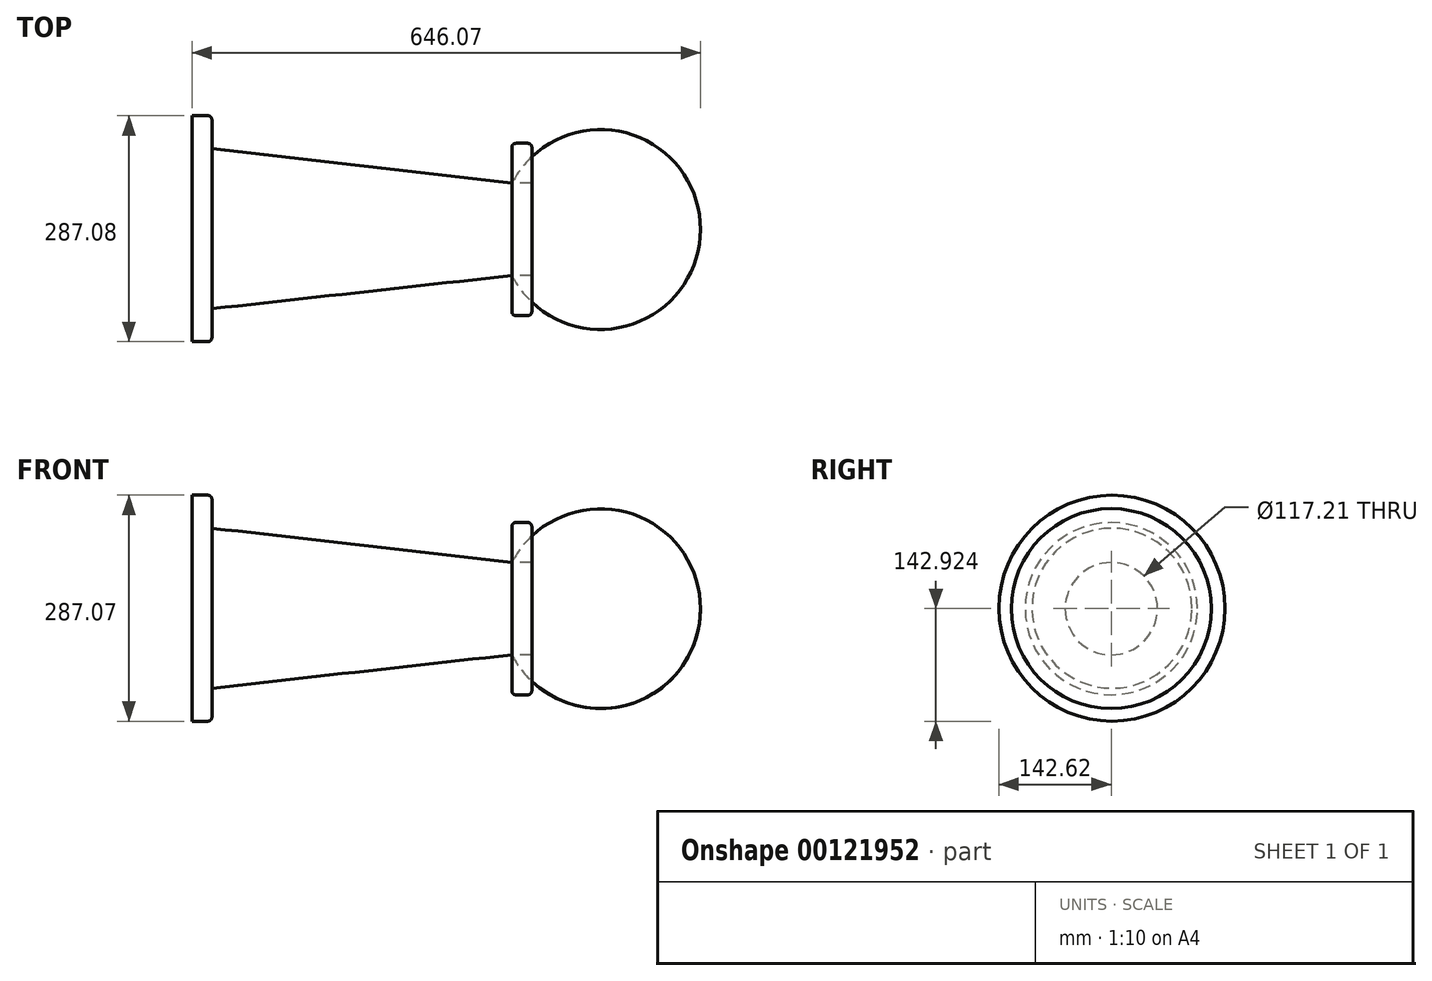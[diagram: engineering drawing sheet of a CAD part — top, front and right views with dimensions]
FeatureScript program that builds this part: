
annotation { "Feature Type Name" : "Feature", "Feature Type Description" : "" }
export const myFeature = defineFeature(function(context is Context, id is Id, definition is map)
    precondition{}
    {
        {
            var Q0;
            Q0=qCreatedBy(makeId("Front.planeOp"),FACE);
            var sketch = newSketch(context, id + "F0", { "sketchPlane" : qUnion([Q0])});
            skLineSegment(sketch, "E0", {"start": v(-47.1, 268.58) * mm, "end": v(-301.1, 268.58) * mm});
            skCircle(sketch, "E1", {"center": v(-174.1, 268.58) * mm, "radius": 127 * mm});
            skLineSegment(sketch, "E2", {"start": v(-286.77, 268.58) * mm, "end": v(-286.77, 327.19) * mm});
            skLineSegment(sketch, "E3", {"start": v(-286.77, 268.58) * mm, "end": v(-286.77, 209.98) * mm});
            skSolve(sketch);
        }
        {
            var Q0;
            {var subQ3=sQuery(id+"F0.wireOp",EDGE,"E3");Q0=makeQuery(id+"F0.imprint","IMPRINT",FACE,{"disambiguationData":[TD([[makeQuery(id+"F0.imprint","IMPRINT",EDGE,{"derivedFrom":subQ3}),1.0]])]});}
            var Q1;
            Q1=sQuery(id+"F0.wireOp",EDGE,"E0");
            revolve(context, id + "F1", {"entities" : qUnion([Q0]), "axis" : qUnion([Q1]), "revolveType" : RevolveType.FULL});
        }
        {
            var Q0;
            Q0=makeQuery(id+"F1.opRevolve","SWEPT_FACE",FACE,{"disambiguationData":[OSD([sQuery(id+"F0.wireOp",EDGE,"E3")])]});
            var sketch = newSketch(context, id + "F2", { "sketchPlane" : qUnion([Q0])});
            skCircle(sketch, "E4", {"center": v(0, 268.58) * mm, "radius": 109.4 * mm});
            skSolve(sketch);
        }
        {
            var Q0;
            Q0=makeQuery(id+"F2.imprint","IMPRINT",FACE,{"disambiguationData":[TD([[makeQuery(id+"F2.imprint","IMPRINT",EDGE,{"derivedFrom":sQuery(id+"F2.wireOp",EDGE,"E4")}),1.0]])]});
            cPlane(context, id + "F3", {"entities" : qUnion([Q0]), "cplaneType" : CPlaneType.OFFSET, "offset" : 381 * mm, "width" : 152.4 * mm, "height" : 152.4 * mm});
        }
        {
            var Q0;
            Q0=qCreatedBy(id+"F3.planeOp",FACE);
            var sketch = newSketch(context, id + "F4", { "sketchPlane" : qUnion([Q0])});
            skCircle(sketch, "E5", {"center": v(-0.92, 269.2) * mm, "radius": 101.6 * mm});
            skSolve(sketch);
        }
        {
            var Q0;
            Q0=makeQuery(id+"F2.imprint","IMPRINT",FACE,{"disambiguationData":[TD([[makeQuery(id+"F2.imprint","IMPRINT",EDGE,{"derivedFrom":sQuery(id+"F2.wireOp",EDGE,"E4")}),1.0]])]});
            extrude(context, id + "F5", {"entities" : qUnion([Q0]), "oppositeDirection" : true, "depth" : 25.4 * mm});
        }
        {
            var Q0;
            Q0=makeQuery(id+"F4.imprint","IMPRINT",FACE,{"disambiguationData":[TD([[makeQuery(id+"F4.imprint","IMPRINT",EDGE,{"derivedFrom":sQuery(id+"F4.wireOp",EDGE,"E5")}),1.0]])]});
            var Q1;
            Q1=makeQuery(id+"F1.opRevolve","SWEPT_FACE",FACE,{"disambiguationData":[OSD([sQuery(id+"F0.wireOp",EDGE,"E3")])]});
            loft(context, id + "F6", {"sheetProfilesArray" : [{ "sheetProfileEntities" : qUnion([Q0]) }, { "sheetProfileEntities" : qUnion([Q1]) }]});
        }
        {
            var Q0;
            Q0=makeQuery(id+"F5.opExtrude","CAP_EDGE",EDGE,{"disambiguationData":[OSD([sQuery(id+"F2.wireOp",EDGE,"E4")])],"isStart":false});
            var Q1;
            Q1=makeQuery(id+"F5.opExtrude","CAP_EDGE",EDGE,{"disambiguationData":[OSD([sQuery(id+"F2.wireOp",EDGE,"E4")])],"isStart":true});
            fillet(context, id + "F7", {"entities" : qUnion([Q0, Q1]), "radius" : 5.08 * mm, "tangentPropagation" : true, "allowEdgeOverflow" : false});
        }
        {
            var Q0;
            Q0=makeQuery(id+"F6.opLoft","CAP_FACE",FACE,{"disambiguationData":[OSD([makeQuery(id+"F4.imprint","IMPRINT",FACE,{"disambiguationData":[TD([[makeQuery(id+"F4.imprint","IMPRINT",EDGE,{"derivedFrom":sQuery(id+"F4.wireOp",EDGE,"E5")}),1.0]])]})])],"isStart":true});
            var sketch = newSketch(context, id + "F8", { "sketchPlane" : qUnion([Q0])});
            skCircle(sketch, "E6", {"center": v(-0.92, 269.2) * mm, "radius": 101.6 * mm});
            skPoint(sketch, "E6.first.point", {"position": v(-74.67, 339.08) * mm});
            skPoint(sketch, "E6.second.point", {"position": v(-44.28, 177.31) * mm});
            skPoint(sketch, "E6.third.point", {"position": v(94.55, 234.45) * mm});
            skCircle(sketch, "E7", {"center": v(-0.92, 269.2) * mm, "radius": 143.54 * mm});
            skSolve(sketch);
        }
        {
            var Q0;
            Q0 = qSketchRegion(id + "F8", true);
            var Q1;
            Q1=makeQuery(id+"F8.imprint","IMPRINT",FACE,{"disambiguationData":[TD([[makeQuery(id+"F8.imprint","IMPRINT",EDGE,{"derivedFrom":sQuery(id+"F8.wireOp",EDGE,"E6")}),1.0]])]});
            extrude(context, id + "F9", {"entities" : qUnion([Q0, Q1]), "depth" : 25.4 * mm});
        }
        {
            var Q0;
            Q0=makeQuery(id+"F9.opExtrude","CAP_EDGE",EDGE,{"disambiguationData":[OSD([sQuery(id+"F8.wireOp",EDGE,"E7")])],"isStart":true});
            fillet(context, id + "F10", {"entities" : qUnion([Q0]), "radius" : 5.08 * mm, "tangentPropagation" : true, "allowEdgeOverflow" : false});
        }
    });
